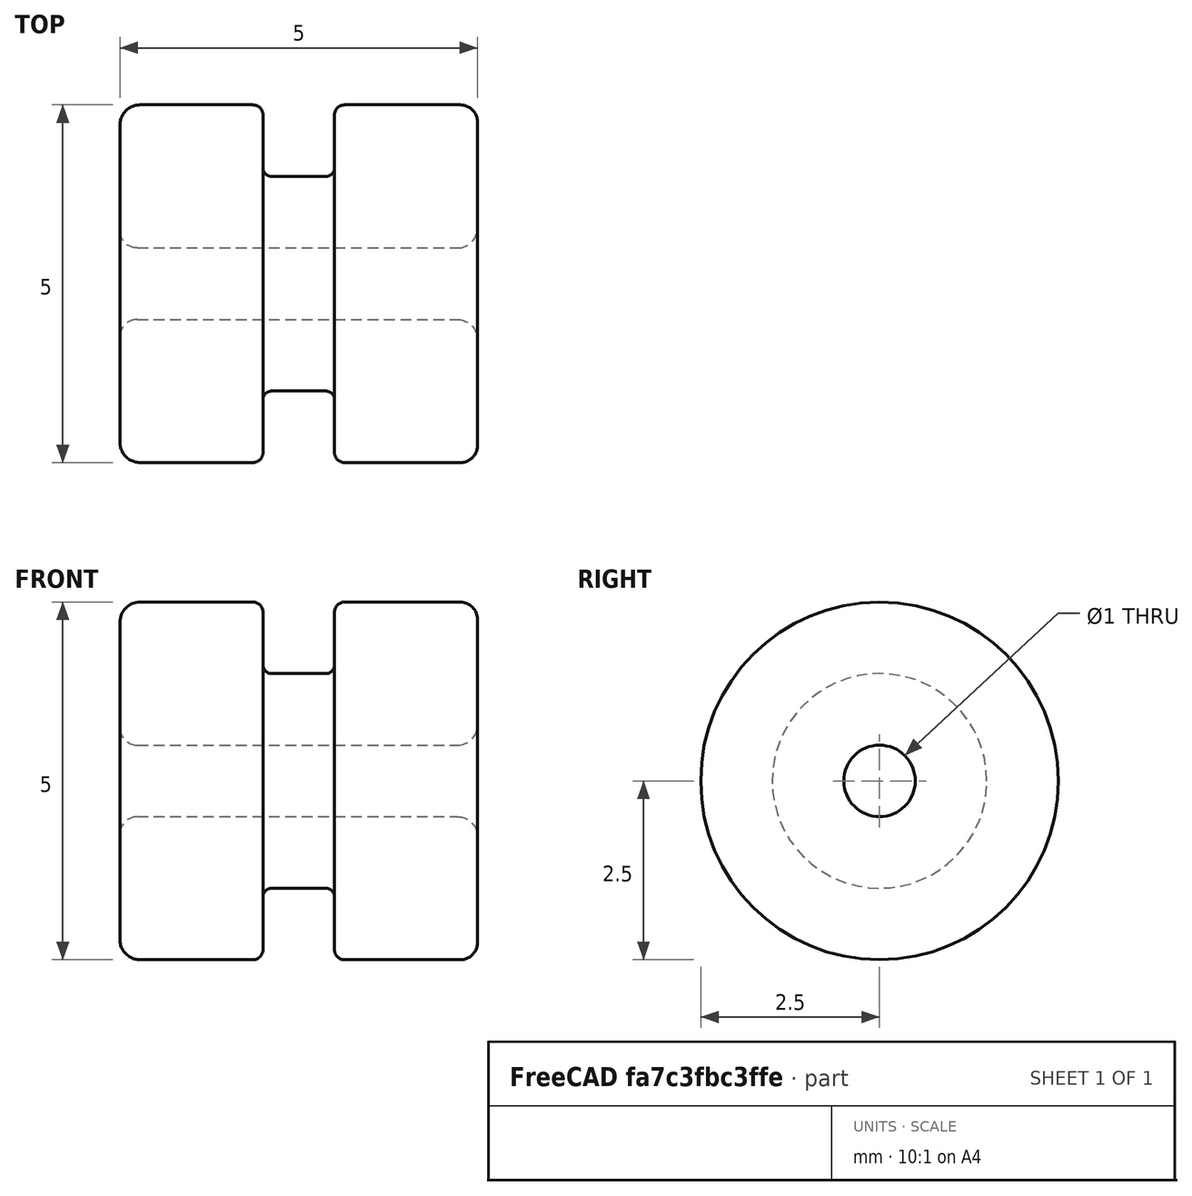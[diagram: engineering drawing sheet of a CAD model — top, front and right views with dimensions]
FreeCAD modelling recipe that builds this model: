
FCSTD DOCUMENT  (FreeCAD 0.20R29177 +426 (Git))
Label: PulleyHand
License: All rights reserved
LicenseURL: http://en.wikipedia.org/wiki/All_rights_reserved
objects: Sketcher::SketchObject×1, Part::Revolution×1, PartDesign::FeatureBase×1, PartDesign::Body×1
note: 4 computed .brp shape members not serialized (recipe doc carries the construction recipe); baked Part::Feature solids carry a one-line shape summary decoded from their .brp

FEATURE [Sketcher::SketchObject] Sketch
  FullyConstrained = false
  MapMode = 5
  Placement = pos=(0,0,0) rot=(1,0,0;1.5708rad)
  Support = -> [XZ_Plane]
  sketch-geometry (16):
    g0: LineSegment StartX=2.5 StartY=0.782843 StartZ=0 EndX=2.5 EndY=2.25716 EndZ=0
    g1: LineSegment StartX=2.25716 StartY=2.5 StartZ=0 EndX=0.641421 EndY=2.5 EndZ=0
    g2: LineSegment StartX=0.5 StartY=2.35858 StartZ=0 EndX=0.5 EndY=1.62142 EndZ=0
    g3: LineSegment StartX=0.378579 StartY=1.5 StartZ=0 EndX=-0.378579 EndY=1.5 EndZ=0
    g4: LineSegment StartX=-0.5 StartY=1.62142 StartZ=0 EndX=-0.5 EndY=2.35858 EndZ=0
    g5: LineSegment StartX=-0.641421 StartY=2.5 StartZ=0 EndX=-2.21716 EndY=2.5 EndZ=0
    g6: LineSegment StartX=-2.5 StartY=2.21716 StartZ=0 EndX=-2.5 EndY=0.742843 EndZ=0
    g7: LineSegment StartX=-2.25716 StartY=0.5 StartZ=0 EndX=2.21716 EndY=0.5 EndZ=0
    g8: ArcOfCircle CenterX=-2.21716 CenterY=2.21716 CenterZ=0 NormalX=0 NormalY=0 NormalZ=1 AngleXU=0 Radius=0.282843 StartAngle=1.5708 EndAngle=3.14159
    g9: ArcOfCircle CenterX=-2.25716 CenterY=0.742843 CenterZ=0 NormalX=0 NormalY=0 NormalZ=1 AngleXU=0 Radius=0.242843 StartAngle=3.14159 EndAngle=4.71239
    g10: ArcOfCircle CenterX=2.21716 CenterY=0.782843 CenterZ=0 NormalX=0 NormalY=0 NormalZ=1 AngleXU=0 Radius=0.282843 StartAngle=4.71239 EndAngle=6.28319
    g11: ArcOfCircle CenterX=2.25716 CenterY=2.25716 CenterZ=0 NormalX=0 NormalY=0 NormalZ=1 AngleXU=0 Radius=0.242843 StartAngle=-9e-16 EndAngle=1.5708
    g12: ArcOfCircle CenterX=0.641421 CenterY=2.35858 CenterZ=0 NormalX=0 NormalY=0 NormalZ=1 AngleXU=0 Radius=0.141421 StartAngle=1.5708 EndAngle=3.14159
    g13: ArcOfCircle CenterX=-0.641421 CenterY=2.35858 CenterZ=0 NormalX=0 NormalY=0 NormalZ=1 AngleXU=0 Radius=0.141421 StartAngle=0 EndAngle=1.5708
    g14: ArcOfCircle CenterX=-0.378579 CenterY=1.62142 CenterZ=0 NormalX=0 NormalY=0 NormalZ=1 AngleXU=0 Radius=0.121421 StartAngle=3.14159 EndAngle=4.71239
    g15: ArcOfCircle CenterX=0.378579 CenterY=1.62142 CenterZ=0 NormalX=0 NormalY=0 NormalZ=1 AngleXU=0 Radius=0.121421 StartAngle=4.71239 EndAngle=6.28319
  constraints (23):
    c: Horizontal(g1)
    c: Vertical(g2)
    c: Horizontal(g3)
    c: Vertical(g4)
    c: Horizontal(g5)
    c: Vertical(g6)
    c: Horizontal(g7)
    c: Tangent(g5,g8) = -1.5708
    c: Tangent(g6,g8) = -1.5708
    c: Tangent(g6,g9) = -1.5708
    c: Tangent(g7,g9) = -1.5708
    c: Tangent(g0,g10) = -1.5708
    c: Tangent(g7,g10) = -1.5708
    c: Tangent(g0,g11) = -1.5708
    c: Tangent(g1,g11) = -1.5708
    c: Tangent(g1,g12) = -1.5708
    c: Tangent(g2,g12) = -1.5708
    c: Tangent(g4,g13) = -1.5708
    c: Tangent(g5,g13) = -1.5708
    c: Tangent(g3,g14) = 1.5708
    c: Tangent(g4,g14) = 1.5708
    c: Tangent(g2,g15) = 1.5708
    c: Tangent(g3,g15) = 1.5708
FEATURE [Part::Revolution] Revolve
  Angle = 360
  Axis = (1,0,0)
  Base = (0,0,0)
  FaceMakerClass = Part::FaceMakerBullseye
  Solid = true
  Source = -> Sketch
  Symmetric = false
FEATURE [PartDesign::FeatureBase] BaseFeature
  BaseFeature = -> Revolve
FEATURE [PartDesign::Body] Body
  BaseFeature = -> Revolve
  Group = -> [BaseFeature,Sketch]
  Origin = -> Origin
  Tip = -> BaseFeature
